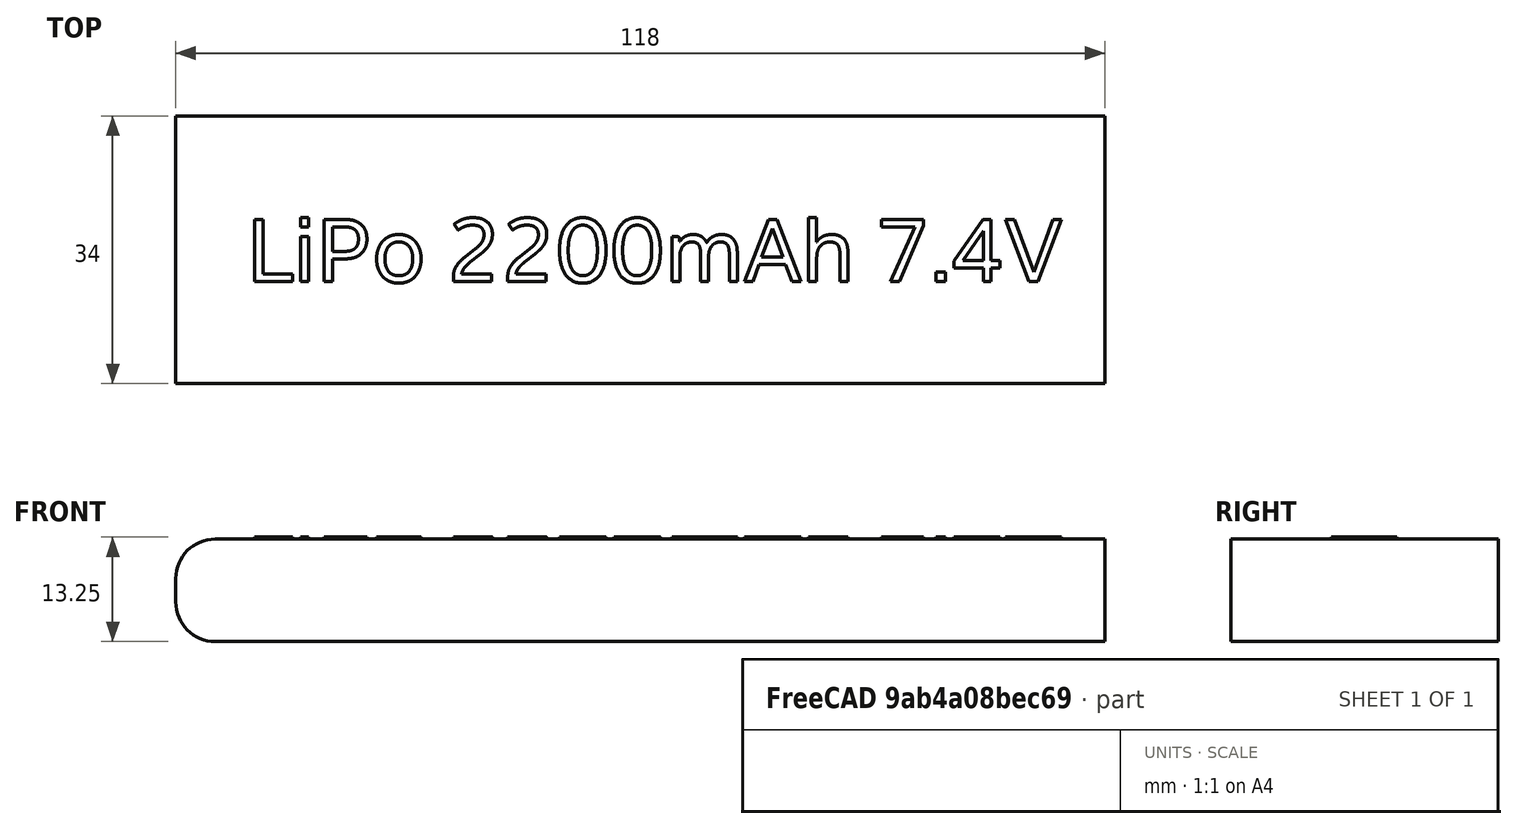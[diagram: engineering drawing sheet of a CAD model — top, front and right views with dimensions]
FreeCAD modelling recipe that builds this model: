
FCSTD DOCUMENT  (FreeCAD 0.18R4 (GitTag))
Label: LiPo_2200mAh
License: All rights reserved
LicenseURL: http://en.wikipedia.org/wiki/All_rights_reserved
objects: Part::Box×1, Part::Fillet×1, Part::Part2DObjectPython×1, Part::Extrusion×1, Part::MultiFuse×1, Part::Feature×1
note: 6 computed .brp shape members not serialized (recipe doc carries the construction recipe); baked Part::Feature solids carry a one-line shape summary decoded from their .brp

FEATURE [Part::Box] Box  label="Cube"
  AttacherType = Attacher::AttachEngine3D
  Height = 13
  Length = 118
  Width = 34
FEATURE [Part::Fillet] Fillet  label="Body"
  Base = -> Box
  Edges = 2 edges r=5: [Edge2,Edge4]
FEATURE [Part::Part2DObjectPython] ShapeString  # Draft 2D object (typed FeaturePython)
  FontFile = <userpath>/Desktop/Intel Clear Arabic Regular.ttf
  Placement = pos=(-76,-12,0) rot=(0,0,1;0rad)
  Size = 10
  String = LiPo 2200mAh 7.4V
  Tracking = 0
FEATURE [Part::Extrusion] Extrude  label="text"
  Base = -> ShapeString
  Dir = (0,0,1)
  DirMode = 2
  FaceMakerClass = Part::FaceMakerBullseye
  LengthFwd = 1
  LengthRev = 0
  Placement = pos=(85,25,12.25) rot=(0,0,1;0rad)
  Solid = false
  Symmetric = false
FEATURE [Part::MultiFuse] Fusion  label="Lipo_2200mAh (Model)"
  Shapes = -> [Fillet,Extrude]
FEATURE [Part::Feature] Fusion_solid  label="Lipo_2200mAh_Model (Solid)"
  shape: bbox 118 x 34 x 13.25 mm, 253 faces (baked)
